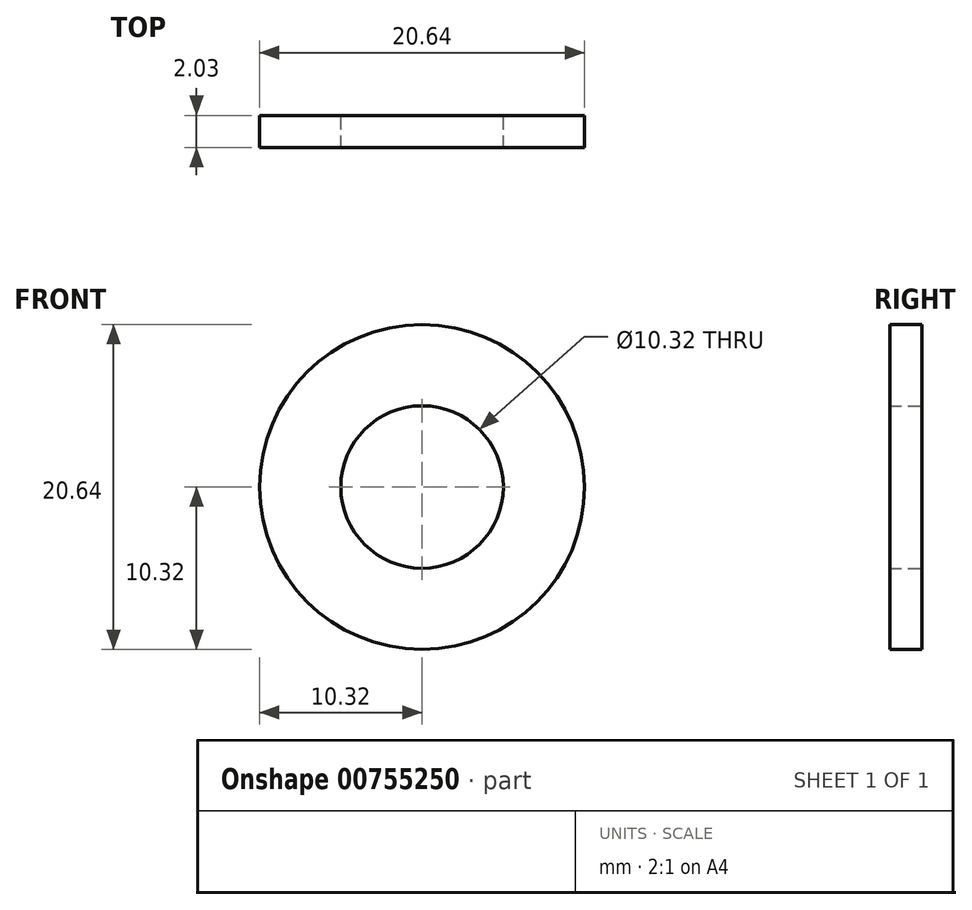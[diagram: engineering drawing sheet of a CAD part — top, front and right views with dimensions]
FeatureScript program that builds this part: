
annotation { "Feature Type Name" : "Feature", "Feature Type Description" : "" }
export const myFeature = defineFeature(function(context is Context, id is Id, definition is map)
    precondition{}
    {
        {
            var Q0;
            Q0=qCreatedBy(makeId("Front.planeOp"),FACE);
            var sketch = newSketch(context, id + "F0", { "sketchPlane" : qUnion([Q0])});
            skCircle(sketch, "E0", {"center": v(0, 0) * mm, "radius": 10.32 * mm});
            skCircle(sketch, "E1", {"center": v(0, 0) * mm, "radius": 5.16 * mm});
            skSolve(sketch);
        }
        {
            var Q0;
            Q0 = qSketchRegion(id + "F0", true);
            extrude(context, id + "F1", {"entities" : qUnion([Q0]), "depth" : 2.03 * mm, "offsetDistance" : 25.4 * mm});
        }
    });
